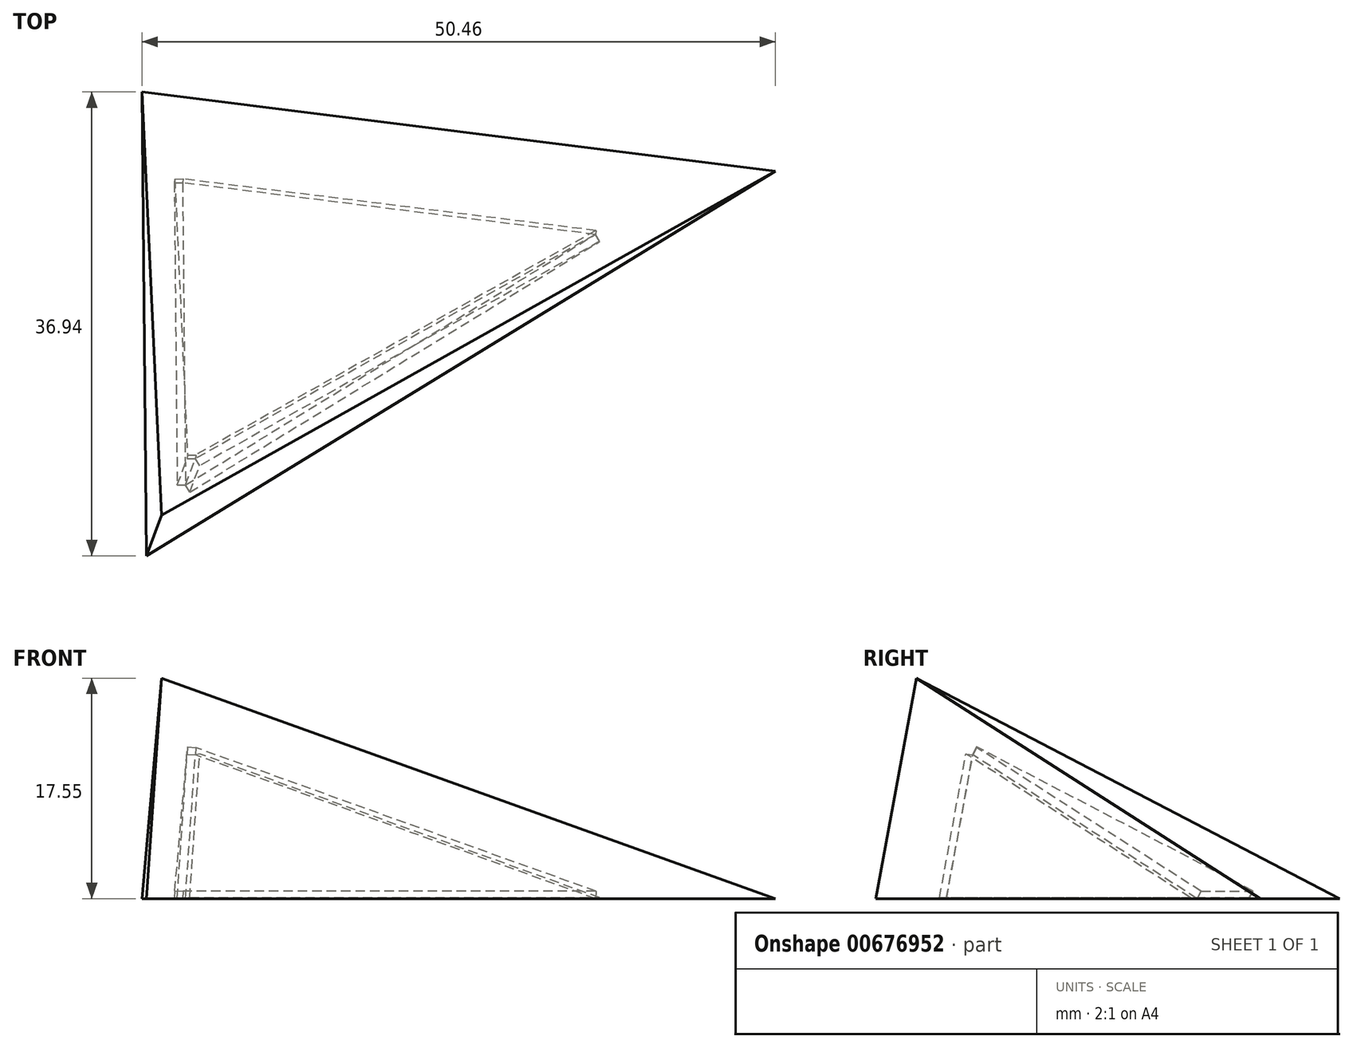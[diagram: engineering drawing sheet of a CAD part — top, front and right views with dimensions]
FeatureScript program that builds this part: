
annotation { "Feature Type Name" : "Feature", "Feature Type Description" : "" }
export const myFeature = defineFeature(function(context is Context, id is Id, definition is map)
    precondition{}
    {
        {
            var Q0;
            Q0=qCreatedBy(makeId("Top.planeOp"),FACE);
            var sketch = newSketch(context, id + "F0", { "sketchPlane" : qUnion([Q0])});
            skLineSegment(sketch, "E0", {"start": v(0, 0) * mm, "end": v(0, 57.74) * mm});
            skLineSegment(sketch, "E1", {"start": v(0, 57.74) * mm, "end": v(100, 57.74) * mm});
            skLineSegment(sketch, "E2", {"start": v(100, 57.74) * mm, "end": v(0, 0) * mm});
            skCircle(sketch, "E3", {"center": v(0, 0) * mm, "radius": 115.47 * mm, "construction": true});
            skLineSegment(sketch, "E4", {"start": v(100, 57.74) * mm, "end": v(-100, 57.74) * mm, "construction": true});
            skLineSegment(sketch, "E5", {"start": v(-100, 57.74) * mm, "end": v(0, -115.47) * mm, "construction": true});
            skSolve(sketch);
        }
        {
            var Q0;
            Q0=qCreatedBy(makeId("Top.planeOp"),FACE);
            cPlane(context, id + "F1", {"entities" : qUnion([Q0]), "cplaneType" : CPlaneType.OFFSET, "offset" : (40 / sqrt(5)) * mm, "width" : 152.4 * mm, "height" : 152.4 * mm});
        }
        {
            var Q0;
            Q0=qCreatedBy(id+"F1.planeOp",FACE);
            var sketch = newSketch(context, id + "F2", { "sketchPlane" : qUnion([Q0])});
            skPoint(sketch, "E6", {"position": v(0, 0) * mm});
            skSolve(sketch);
        }
        {
            var Q0;
            Q0=makeQuery(id+"F0.imprint","IMPRINT",FACE,{"disambiguationData":[TD([[makeQuery(id+"F0.imprint","IMPRINT",EDGE,{"derivedFrom":sQuery(id+"F0.wireOp",EDGE,"E0")}),-1.0]])]});
            var Q1;
            Q1=sQuery(id+"F2.wireOp",VERTEX,"E6");
            loft(context, id + "F3", {"sheetProfilesArray" : [{ "sheetProfileEntities" : qUnion([Q0]) }, { "sheetProfileEntities" : qUnion([Q1]) }]});
        }
        {
            var Q0;
            Q0=makeQuery(id+"F3.opLoft","SWEPT_BODY",BODY,{"disambiguationData":[OSD([makeQuery(id+"F0.imprint","IMPRINT",FACE,{"disambiguationData":[TD([[makeQuery(id+"F0.imprint","IMPRINT",EDGE,{"derivedFrom":sQuery(id+"F0.wireOp",EDGE,"E0")}),-1.0]])]}),sQuery(id+"F2.wireOp",VERTEX,"E6")])]});
            var Q1;
            {var subQ0=sQuery(id+"F0.wireOp",EDGE,"E0");var subQ1=sQuery(id+"F0.wireOp",EDGE,"E1");var subQ2=sQuery(id+"F0.wireOp",EDGE,"E2");Q1=makeQuery(id+"F3.opLoft","MID_CAP_EDGE",EDGE,{"disambiguationData":[OSD([subQ0,subQ1,subQ2]),TDD([makeQuery(id+"F0.imprint","INTERSECT",VERTEX,{"derivedFrom":[subQ0,subQ2]}),makeQuery(id+"F0.imprint","INTERSECT",VERTEX,{"derivedFrom":[subQ0,subQ1]}),makeQuery(id+"F0.imprint","IMPRINT",EDGE,{"derivedFrom":subQ0})])],"capPos":0.0});}
            transform(context, id + "F4", {"entities" : qUnion([Q0]), "transformType" : TransformType.ROTATION, "transformAxis" : qUnion([Q1]), "angle" : 10 * degree, "makeCopy" : false});
        }
        {
            var Q0;
            Q0=makeQuery(id+"F3.opLoft","SWEPT_BODY",BODY,{"disambiguationData":[OSD([makeQuery(id+"F0.imprint","IMPRINT",FACE,{"disambiguationData":[TD([[makeQuery(id+"F0.imprint","IMPRINT",EDGE,{"derivedFrom":sQuery(id+"F0.wireOp",EDGE,"E0")}),-1.0]])]}),sQuery(id+"F2.wireOp",VERTEX,"E6")])]});
            var Q1;
            {var subQ0=sQuery(id+"F0.wireOp",EDGE,"E2");var subQ1=sQuery(id+"F0.wireOp",EDGE,"E1");var subQ2=sQuery(id+"F0.wireOp",EDGE,"E0");Q1=makeQuery(id+"F3.opLoft","MID_CAP_EDGE",EDGE,{"disambiguationData":[OSD([subQ2,subQ1,subQ0]),TDD([makeQuery(id+"F0.imprint","INTERSECT",VERTEX,{"derivedFrom":[subQ2,subQ0]}),makeQuery(id+"F0.imprint","INTERSECT",VERTEX,{"derivedFrom":[subQ1,subQ0]}),makeQuery(id+"F0.imprint","IMPRINT",EDGE,{"derivedFrom":subQ0})])],"capPos":0.0});}
            transform(context, id + "F5", {"entities" : qUnion([Q0]), "transformType" : TransformType.ROTATION, "transformAxis" : qUnion([Q1]), "angle" : 12 * degree, "makeCopy" : false});
        }
        {
            var Q0;
            Q0=qCreatedBy(makeId("Top.planeOp"),FACE);
            var sketch = newSketch(context, id + "F6", { "sketchPlane" : qUnion([Q0])});
            skCircle(sketch, "E7", {"center": v(-179.78, 43.82) * mm, "radius": 108.52 * mm});
            skSolve(sketch);
        }
        {
            var Q0;
            Q0=makeQuery(id+"F6.imprint","IMPRINT",FACE,{"disambiguationData":[TD([[makeQuery(id+"F6.imprint","IMPRINT",EDGE,{"derivedFrom":sQuery(id+"F6.wireOp",EDGE,"E7")}),1.0]])]});
            var Q1;
            Q1=sQuery(id+"F6.wireOp",EDGE,"E7");
            extrude(context, id + "F7", {"entities" : qUnion([Q0]), "surfaceEntities" : qUnion([Q1]), "depth" : 101 * mm, "offsetDistance" : 25.4 * mm});
        }
        {
            var Q0;
            Q0=makeQuery(id+"F7.opExtrude","SWEPT_BODY",BODY,{"disambiguationData":[OSD([sQuery(id+"F6.wireOp",EDGE,"E7")])]});
            transform(context, id + "F8", {"entities" : qUnion([Q0]), "transformType" : TransformType.TRANSLATION_3D, "dx" : 177.04 * mm, "dy" : 0 * mm, "dz" : 0 * mm, "makeCopy" : false});
        }
        {
            var Q0;
            Q0=makeQuery(id+"F3.opLoft","SWEPT_BODY",BODY,{"disambiguationData":[OSD([makeQuery(id+"F0.imprint","IMPRINT",FACE,{"disambiguationData":[TD([[makeQuery(id+"F0.imprint","IMPRINT",EDGE,{"derivedFrom":sQuery(id+"F0.wireOp",EDGE,"E0")}),-1.0]])]}),sQuery(id+"F2.wireOp",VERTEX,"E6")])]});
            var Q1;
            Q1=makeQuery(id+"F7.opExtrude","SWEPT_BODY",BODY,{"disambiguationData":[OSD([sQuery(id+"F6.wireOp",EDGE,"E7")])]});
            booleanBodies(context, id + "F9", {"operationType" : BooleanOperationType.INTERSECTION, "tools" : qUnion([Q0, Q1])});
        }
        {
            var Q0;
            Q0=makeQuery(id+"F7.opExtrude","CAP_FACE",FACE,{"disambiguationData":[OSD([sQuery(id+"F6.wireOp",EDGE,"E7")])],"isStart":true});
            var Q1;
            Q1=makeQuery(id+"F7.opExtrude","CAP_FACE",FACE,{"disambiguationData":[OSD([sQuery(id+"F6.wireOp",EDGE,"E7")])],"isStart":false});
            shell(context, id + "F10", {"entities" : qUnion([Q0, Q1]), "thickness" : 0.66 * mm + 2.5 * mm});
        }
        {
            var Q0;
            {var subQ0=sQuery(id+"F0.wireOp",EDGE,"E0");var subQ1=sQuery(id+"F0.wireOp",EDGE,"E1");var subQ2=sQuery(id+"F0.wireOp",EDGE,"E2");Q0=makeQuery(id+"F10.opShell","OFFSET_FACE",FACE,{"disambiguationData":[OSD([subQ0,subQ1,subQ2]),TDD([makeQuery(id+"F3.opLoft","SWEPT_FACE",FACE,{"disambiguationData":[OSD([subQ0,subQ1,subQ2]),TDD([makeQuery(id+"F0.imprint","INTERSECT",VERTEX,{"derivedFrom":[subQ0,subQ2]}),makeQuery(id+"F0.imprint","INTERSECT",VERTEX,{"derivedFrom":[subQ0,subQ1]}),makeQuery(id+"F0.imprint","IMPRINT",EDGE,{"derivedFrom":subQ0})])]})])]});}
            extrude(context, id + "F11", {"entities" : qUnion([Q0]), "operationType" : NewBodyOperationType.REMOVE, "oppositeDirection" : true, "depth" : 0.66 * mm, "offsetDistance" : 25.4 * mm});
        }
        {
            var Q0;
            {var subQ0=sQuery(id+"F0.wireOp",EDGE,"E2");var subQ1=sQuery(id+"F0.wireOp",EDGE,"E1");var subQ2=sQuery(id+"F0.wireOp",EDGE,"E0");Q0=makeQuery(id+"F10.opShell","OFFSET_FACE",FACE,{"disambiguationData":[OSD([subQ2,subQ1,subQ0]),TDD([makeQuery(id+"F3.opLoft","SWEPT_FACE",FACE,{"disambiguationData":[OSD([subQ2,subQ1,subQ0]),TDD([makeQuery(id+"F0.imprint","INTERSECT",VERTEX,{"derivedFrom":[subQ2,subQ0]}),makeQuery(id+"F0.imprint","INTERSECT",VERTEX,{"derivedFrom":[subQ1,subQ0]}),makeQuery(id+"F0.imprint","IMPRINT",EDGE,{"derivedFrom":subQ0})])]})])]});}
            extrude(context, id + "F12", {"entities" : qUnion([Q0]), "operationType" : NewBodyOperationType.REMOVE, "oppositeDirection" : true, "depth" : 0.66 * mm, "offsetDistance" : 25.4 * mm});
        }
        {
            var Q0;
            {var subQ0=sQuery(id+"F0.wireOp",EDGE,"E1");var subQ1=sQuery(id+"F0.wireOp",EDGE,"E0");var subQ2=sQuery(id+"F0.wireOp",EDGE,"E2");Q0=makeQuery(id+"F11.boolean.opBoolean","MERGE",FACE,{"derivedFrom":[makeQuery(id+"F10.opShell","OFFSET_FACE",FACE,{"disambiguationData":[OSD([subQ1,subQ0,subQ2]),TDD([makeQuery(id+"F3.opLoft","SWEPT_FACE",FACE,{"disambiguationData":[OSD([subQ1,subQ0,subQ2]),TDD([makeQuery(id+"F0.imprint","INTERSECT",VERTEX,{"derivedFrom":[subQ1,subQ0]}),makeQuery(id+"F0.imprint","INTERSECT",VERTEX,{"derivedFrom":[subQ0,subQ2]}),makeQuery(id+"F0.imprint","IMPRINT",EDGE,{"derivedFrom":subQ0})])]})])]}),makeQuery(id+"F11.opExtrude","SWEPT_FACE",FACE,{"disambiguationData":[OSD([subQ1,subQ0,sQuery(id+"F2.wireOp",VERTEX,"E6")])]})]});}
            extrude(context, id + "F13", {"entities" : qUnion([Q0]), "operationType" : NewBodyOperationType.REMOVE, "oppositeDirection" : true, "depth" : 0.66 * mm, "offsetDistance" : 25.4 * mm});
        }
        {
            var Q0;
            Q0=makeQuery(id+"F9.opBoolean","INTERSECT",BODY,{"derivedFrom":[makeQuery(id+"F3.opLoft","SWEPT_BODY",BODY,{"disambiguationData":[OSD([makeQuery(id+"F0.imprint","IMPRINT",FACE,{"disambiguationData":[TD([[makeQuery(id+"F0.imprint","IMPRINT",EDGE,{"derivedFrom":sQuery(id+"F0.wireOp",EDGE,"E0")}),-1.0]])]}),sQuery(id+"F2.wireOp",VERTEX,"E6")])]}),makeQuery(id+"F7.opExtrude","SWEPT_BODY",BODY,{"disambiguationData":[OSD([sQuery(id+"F6.wireOp",EDGE,"E7")])]})]});
            transform(context, id + "F14", {"entities" : qUnion([Q0]), "transformType" : TransformType.TRANSLATION_3D, "dx" : 0 * mm, "dy" : 0 * mm, "dz" : -1 * mm, "makeCopy" : false});
        }
    });
